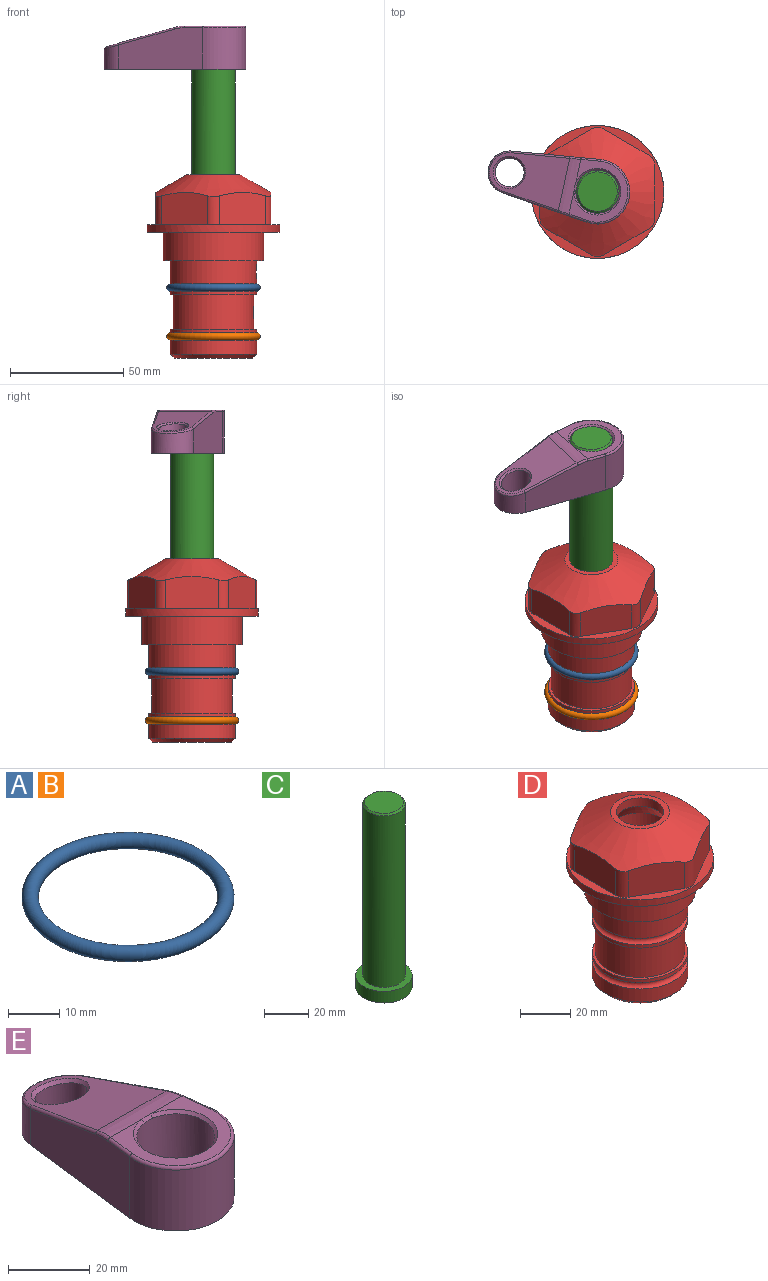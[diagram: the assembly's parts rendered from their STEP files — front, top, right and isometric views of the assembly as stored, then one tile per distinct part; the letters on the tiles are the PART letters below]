
ASSEMBLY  parts=5 mates=4
PART A: 1 faces, bbox 44.7x44.7x3.2 mm
  f0: torus R=19.05mm, axis (0,0,1), area 1193.9mm2
PART B: same geometry as A
PART C: 6 faces, bbox 25.4x25.4x101.6 mm
  f0: plane 17.46x17.46mm, normal (0,0,1), area 239.5mm2, adj f5
  f1: plane 25.4x25.4mm, normal (0,0,-1), area 506.7mm2, adj f2
  f2: cylinder r=12.7mm len=25.4mm, axis (0,0,1), area 506.7mm2, adj f1,f3
  f3: plane 25.4x25.4mm, normal (0,0,1), area 221.7mm2, adj f2,f4
  f4: cylinder r=9.53mm len=94.46mm, axis (0,0,1), area 5653mm2, adj f3,f5
  f5: cone r=8.73mm half-angle=45deg, axis (0,0,-1), area 64.4mm2, adj f0,f4
PART D: 36 faces, bbox 58.7x58.7x81 mm
  f0: cylinder r=17.78mm len=35.56mm, axis (0,0,1), area 1670.8mm2, adj f23,f24,f31
  f1: cylinder r=19.05mm len=38.1mm, axis (0,0,1), area 1191.9mm2, adj f26,f27,f30
  f2: plane 58.66x58.66mm, normal (0,0,-1), area 1150.6mm2, adj f3,f28
  f3: cylinder r=29.33mm len=58.66mm, axis (0,0,-1), area 585.1mm2, adj f2,f4
  f4: plane 58.66x58.66mm, normal (0,0,1), area 475.9mm2, adj f3,f5,f6,f7,f8,f9,f10,f11
  f5: plane 20.32x14.34mm, normal (-0.5,0.87,0), area 324.4mm2, adj f4,f15,f16,f17
  f6: plane 20.32x14.34mm, normal (0.5,0.87,0), area 324.4mm2, adj f4,f14,f15,f17
  f7: plane 23.48x14.34mm, normal (1,0,0), area 324.4mm2, adj f4,f13,f14,f17
  f8: plane 20.32x14.34mm, normal (0.5,-0.87,0), area 324.4mm2, adj f4,f12,f13,f17
  f9: plane 20.32x14.34mm, normal (-0.5,-0.87,0), area 324.4mm2, adj f4,f11,f12,f17
  f10: plane 23.48x14.34mm, normal (-1,0,0), area 324.4mm2, adj f4,f11,f16,f17
  f11: cylinder r=5.08mm len=12.85mm, axis (0,0,-1), area 67.2mm2, adj f4,f9,f10,f17
  f12: cylinder r=5.08mm len=12.85mm, axis (0,0,-1), area 67.2mm2, adj f4,f8,f9,f17
  f13: cylinder r=5.08mm len=12.85mm, axis (0,0,-1), area 67.2mm2, adj f4,f7,f8,f17
  f14: cylinder r=5.08mm len=12.85mm, axis (0,0,-1), area 67.2mm2, adj f4,f6,f7,f17
  f15: cylinder r=5.08mm len=12.85mm, axis (0,0,-1), area 67.2mm2, adj f4,f5,f6,f17
  f16: cylinder r=5.08mm len=12.85mm, axis (0,0,-1), area 67.2mm2, adj f4,f5,f10,f17
  f17: cone r=11.73mm half-angle=60deg, axis (0,0,-1), area 2071.8mm2, adj f5,f6,f7,f8,f9,f10,f11,f12
  f18: plane 23.46x23.46mm, normal (0,0,1), area 147.4mm2, adj f17,f35
  f19: plane 34.93x34.93mm, normal (0,0,-1), area 958mm2, adj f29
  f20: cylinder r=19.05mm len=38.1mm, axis (0,0,1), area 760.1mm2, adj f21,f29
  f21: torus R=19.05mm, axis (0,0,1), area 565.3mm2, adj f20,f22
  f22: cylinder r=19.05mm len=38.1mm, axis (0,0,1), area 190mm2, adj f21,f23
  f23: plane 38.1x38.1mm, normal (0,0,1), area 146.9mm2, adj f0,f22
  f24: plane 38.1x38.1mm, normal (0,0,-1), area 146.9mm2, adj f0,f25
  f25: cylinder r=19.05mm len=38.1mm, axis (0,0,1), area 190mm2, adj f24,f26
  f26: torus R=19.05mm, axis (0,0,1), area 565.3mm2, adj f1,f25
  f27: plane 44.45x44.45mm, normal (0,0,-1), area 411.7mm2, adj f1,f28
  f28: cylinder r=22.23mm len=44.45mm, axis (0,0,1), area 1773.5mm2, adj f2,f27
  f29: cone r=19.05mm half-angle=45deg, axis (0,0,1), area 257.5mm2, adj f19,f20
  f30: cylinder r=3.17mm len=6.75mm, axis (-1,0,0), area 128mm2, adj f1,f33
  f31: cylinder r=3.17mm len=6.35mm, axis (-1,0,0), area 102.5mm2, adj f0,f33
  f32: plane 25.4x25.4mm, normal (0,0,1), area 506.7mm2, adj f33
  f33: cylinder r=12.7mm len=66.42mm, axis (0,0,-1), area 5236.2mm2, adj f30,f31,f32,f34
  f34: cone r=9.53mm half-angle=30deg, axis (0,0,-1), area 443.4mm2, adj f33,f35
  f35: cylinder r=9.53mm len=19.05mm, axis (0,0,-1), area 240.9mm2, adj f18,f34
PART E: 31 faces, bbox 31.7x65.5x19.8 mm
  f0: plane 39.12x18.26mm, normal (0.99,0.12,0), area 612.2mm2, adj f1,f4,f7,f11,f13,f15
  f1: cylinder r=9.53mm len=18.91mm, axis (0,0,-1), area 296.1mm2, adj f0,f2,f7,f17
  f2: plane 39.12x18.26mm, normal (-0.99,0.12,0), area 612.2mm2, adj f1,f4,f7,f12,f14,f16
  f3: cylinder r=6.35mm len=12.7mm, axis (0,0,-1), area 362.4mm2, adj f7,f18
  f4: cylinder r=14.29mm len=28.58mm, axis (0,0,-1), area 882.2mm2, adj f0,f2,f7,f10
  f5: cylinder r=9.53mm len=19.05mm, axis (0,0,-1), area 1092.6mm2, adj f7,f19,f20
  f6: plane 26.99x23.69mm, normal (0,0,1), area 216.2mm2, adj f9,f10,f11,f12,f19
  f7: plane 63.5x28.58mm, normal (0,0,-1), area 661.8mm2, adj f0,f1,f2,f3,f4,f5,f22,f23
  f8: plane 33.52x23.6mm, normal (0,0.26,0.97), area 486mm2, adj f9,f15,f16,f17,f18
  f9: cylinder r=19.05mm len=24.72mm, axis (1,0,0), area 120.4mm2, adj f6,f8,f13,f14,f20
  f10: torus R=13.49mm, axis (0,0,1), area 59mm2, adj f4,f6,f11,f12
  f11: cylinder r=0.79mm len=8.67mm, axis (0.12,-0.99,0), area 10.8mm2, adj f0,f6,f10,f13
  f12: cylinder r=0.79mm len=8.67mm, axis (0.12,0.99,0), area 10.8mm2, adj f2,f6,f10,f14
  f13: bspline ~4.95x1.42mm, area 6.1mm2, adj f0,f9,f11,f15
  f14: bspline ~4.95x1.42mm, area 6.1mm2, adj f2,f9,f12,f16
  f15: cylinder r=0.79mm len=25.95mm, axis (0.12,-0.96,0.26), area 32.9mm2, adj f0,f8,f13,f17
  f16: cylinder r=0.79mm len=25.95mm, axis (0.12,0.96,-0.26), area 32.9mm2, adj f2,f8,f14,f17
  f17: bspline ~18.91x8.38mm, area 30mm2, adj f1,f8,f15,f16
  f18: bspline ~14.29x14.29mm, area 48.3mm2, adj f3,f8
  f19: cone r=9.53mm half-angle=45deg, axis (0,0,1), area 66.5mm2, adj f5,f6,f20
  f20: bspline ~3.22x0.96mm, area 3.5mm2, adj f5,f9,f19
  f21: plane 2.75x2.72mm, normal (0,0,-1), area 2.9mm2, adj f23,f25,f28
  f22: plane 23.05x15.88mm, normal (-0.99,-0.12,0), area 323.6mm2, adj f7,f25,f26,f27,f28,f29
  f23: plane 23.05x15.88mm, normal (0.99,-0.12,0), area 323.6mm2, adj f7,f21,f25,f27,f28,f30
  f24: cylinder r=9.53mm len=10.69mm, axis (0,0,-1), area 114.7mm2, adj f7,f27,f29,f30
  f25: cylinder r=12.7mm len=20.59mm, axis (0,0,-1), area 381.1mm2, adj f7,f21,f22,f23,f26,f28
  f26: plane 2.75x2.72mm, normal (0,0,-1), area 2.9mm2, adj f22,f25,f28
  f27: plane 19.72x18.37mm, normal (0,-0.26,-0.97), area 291.8mm2, adj f22,f23,f24,f28,f29,f30
  f28: cylinder r=15.88mm len=19.92mm, axis (1,0,0), area 54.8mm2, adj f21,f22,f23,f25,f26,f27
  f29: cylinder r=1.59mm len=11mm, axis (0,0,-1), area 34.7mm2, adj f7,f22,f24,f27
  f30: cylinder r=1.59mm len=11mm, axis (0,0,-1), area 34.7mm2, adj f7,f23,f24,f27
PLACE A at identity
PLACE B t=(0,0,-21.59)mm
PLACE C rot(axis=(0,0,1),77.7deg) t=(0,0,27.55)mm
PLACE D at identity fixed
PLACE E rot(axis=(0,0,1),77.7deg) t=(0,0,27.55)mm
MATE fastened A.f0 <-> D.f0  axis (0,0,1) through (0,0,-24.51)mm
MATE fastened B.f0 <-> D.f0  axis (0,0,1) through (0,0,-46.1)mm
MATE fastened C.f2 <-> E.f4  axis (0,0,1) through (0,0,90.26)mm
MATE cylindrical C.f2 <-> D.f0  axis (0,0,-1) through (0,0,-10.55)mm
